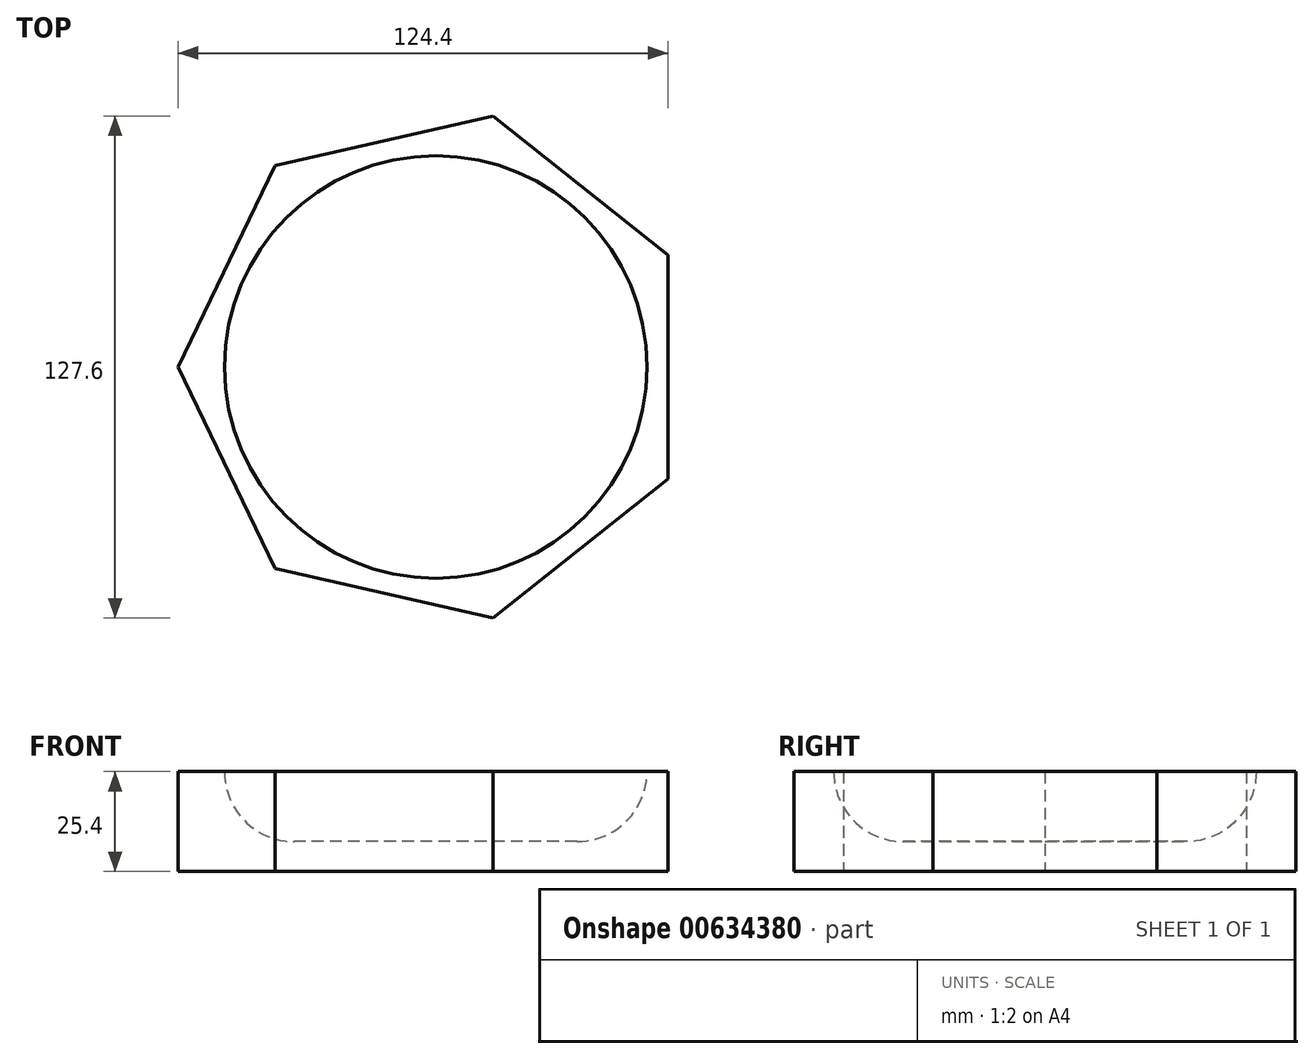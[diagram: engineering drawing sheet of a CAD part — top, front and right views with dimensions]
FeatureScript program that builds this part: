
annotation { "Feature Type Name" : "Feature", "Feature Type Description" : "" }
export const myFeature = defineFeature(function(context is Context, id is Id, definition is map)
    precondition{}
    {
        {
            var Q0;
            Q0=qCreatedBy(makeId("Top.planeOp"),FACE);
            var sketch = newSketch(context, id + "F0", { "sketchPlane" : qUnion([Q0])});
            skCircle(sketch, "E0.cCircle", {"center": v(0, 0) * mm, "radius": 58.96 * mm, "construction": true});
            skLineSegment(sketch, "E0.0", {"start": v(58.96, 28.4) * mm, "end": v(58.96, -28.4) * mm});
            skLineSegment(sketch, "E0.1", {"start": v(58.96, -28.4) * mm, "end": v(14.56, -63.8) * mm});
            skLineSegment(sketch, "E0.2", {"start": v(14.56, -63.8) * mm, "end": v(-40.8, -51.16) * mm});
            skLineSegment(sketch, "E0.3", {"start": v(-40.8, -51.16) * mm, "end": v(-65.44, 0) * mm});
            skLineSegment(sketch, "E0.4", {"start": v(-65.44, 0) * mm, "end": v(-40.8, 51.16) * mm});
            skLineSegment(sketch, "E0.5", {"start": v(-40.8, 51.16) * mm, "end": v(14.56, 63.8) * mm});
            skLineSegment(sketch, "E0.6", {"start": v(14.56, 63.8) * mm, "end": v(58.96, 28.4) * mm});
            skPoint(sketch, "E0.0.midPoint", {"position": v(58.96, 0) * mm});
            skSolve(sketch);
        }
        {
            var Q0;
            Q0=makeQuery(id+"F0.imprint","IMPRINT",FACE,{"disambiguationData":[TD([[makeQuery(id+"F0.imprint","IMPRINT",EDGE,{"derivedFrom":sQuery(id+"F0.wireOp",EDGE,"E0.0")}),-1.0]])]});
            extrude(context, id + "F1", {"entities" : qUnion([Q0]), "depth" : 25.4 * mm, "offsetDistance" : 25.4 * mm});
        }
        {
            var Q0;
            Q0=makeQuery(id+"F1.opExtrude","CAP_FACE",FACE,{"disambiguationData":[OSD([sQuery(id+"F0.wireOp",EDGE,"E0.0"),sQuery(id+"F0.wireOp",EDGE,"E0.1"),sQuery(id+"F0.wireOp",EDGE,"E0.2"),sQuery(id+"F0.wireOp",EDGE,"E0.3"),sQuery(id+"F0.wireOp",EDGE,"E0.4"),sQuery(id+"F0.wireOp",EDGE,"E0.5"),sQuery(id+"F0.wireOp",EDGE,"E0.6")])],"isStart":false});
            var sketch = newSketch(context, id + "F2", { "sketchPlane" : qUnion([Q0])});
            skCircle(sketch, "E1", {"center": v(0, 0) * mm, "radius": 53.67 * mm});
            skSolve(sketch);
        }
        {
            var Q0;
            Q0=makeQuery(id+"F2.imprint","IMPRINT",FACE,{"disambiguationData":[TD([[makeQuery(id+"F2.imprint","IMPRINT",EDGE,{"derivedFrom":sQuery(id+"F2.wireOp",EDGE,"E1")}),1.0]])]});
            extrude(context, id + "F3", {"entities" : qUnion([Q0]), "operationType" : NewBodyOperationType.REMOVE, "oppositeDirection" : true, "depth" : 17.78 * mm, "offsetDistance" : 25.4 * mm});
        }
        {
            var Q0;
            Q0=makeQuery(id+"F3.boolean.opBoolean","COPY",EDGE,{"derivedFrom":makeQuery(id+"F3.opExtrude","CAP_EDGE",EDGE,{"disambiguationData":[OSD([sQuery(id+"F2.wireOp",EDGE,"E1")])],"isStart":false})});
            fillet(context, id + "F4", {"entities" : qUnion([Q0]), "radius" : 17.78 * mm, "tangentPropagation" : true, "allowEdgeOverflow" : false});
        }
    });
